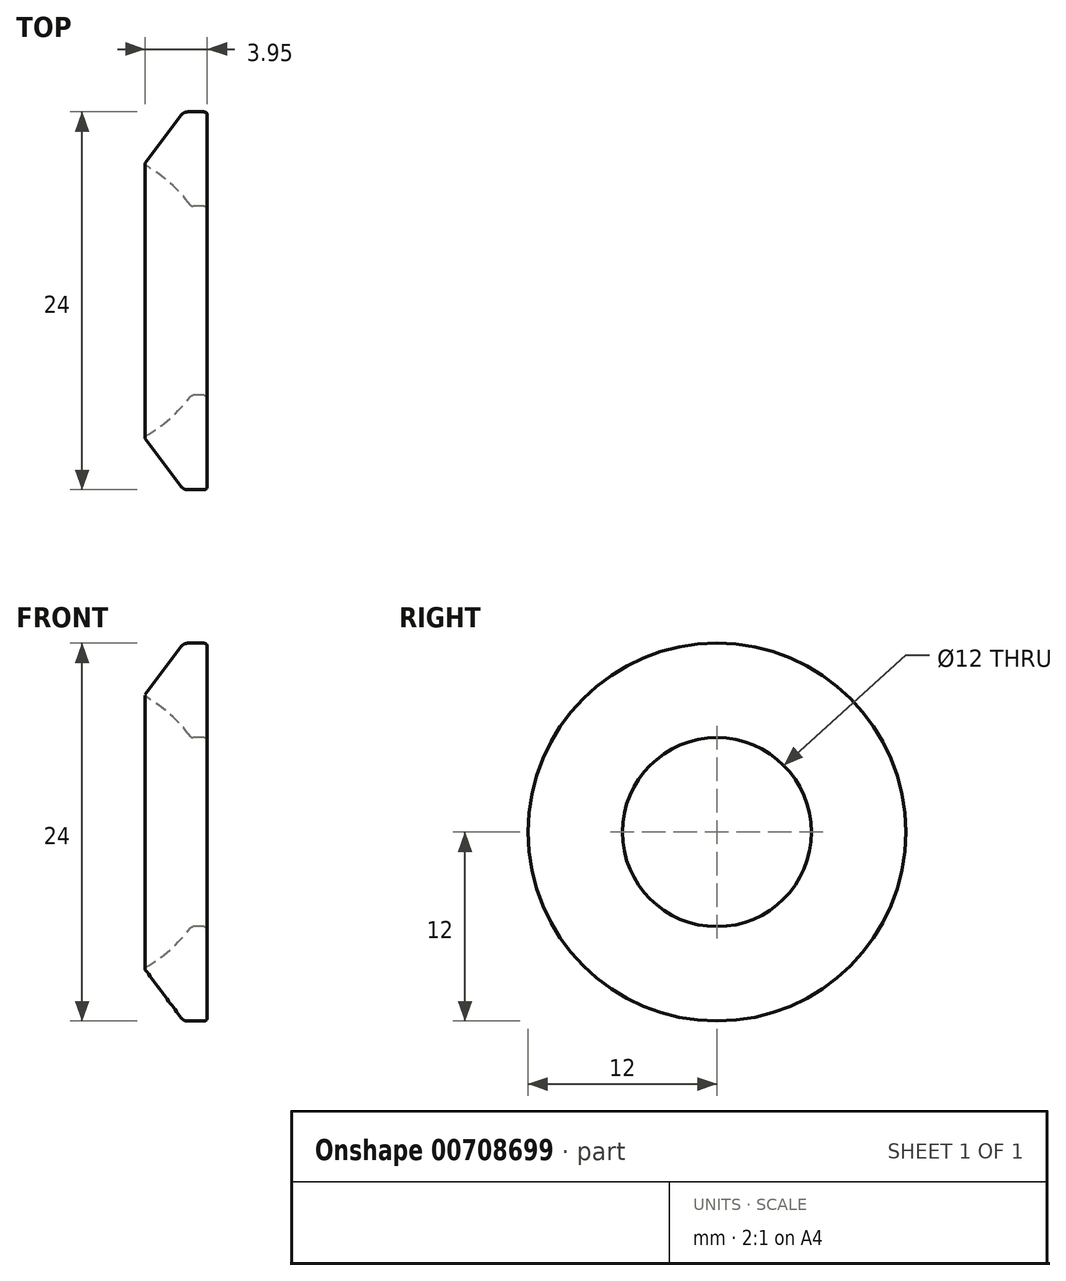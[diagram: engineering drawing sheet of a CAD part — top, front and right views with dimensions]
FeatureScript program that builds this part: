
annotation { "Feature Type Name" : "Feature", "Feature Type Description" : "" }
export const myFeature = defineFeature(function(context is Context, id is Id, definition is map)
    precondition{}
    {
        {
            var Q0;
            Q0=qCreatedBy(makeId("Front.planeOp"),FACE);
            var sketch = newSketch(context, id + "F0", { "sketchPlane" : qUnion([Q0])});
            skLineSegment(sketch, "E0", {"start": v(-1, 6) * mm, "end": v(0, 6) * mm});
            skLineSegment(sketch, "E1", {"start": v(0, 6) * mm, "end": v(0, 12) * mm});
            skLineSegment(sketch, "E2", {"start": v(0, 12) * mm, "end": v(-1.5, 12) * mm});
            skLineSegment(sketch, "E3", {"start": v(-1.5, 12) * mm, "end": v(-4, 8.66) * mm});
            skArc(sketch, "E4", {"start": v(-4, 8.66) * mm, "mid": v(-2.37, 7.48) * mm, "end": v(-1, 6) * mm});
            skLineSegment(sketch, "E5", {"start": v(-16.9, 0) * mm, "end": v(12.5, 0) * mm, "construction": true});
            skSolve(sketch);
        }
        {
            var Q0;
            Q0=makeQuery(id+"F0.imprint","IMPRINT",FACE,{"disambiguationData":[TD([[makeQuery(id+"F0.imprint","IMPRINT",EDGE,{"derivedFrom":sQuery(id+"F0.wireOp",EDGE,"E0")}),1.0]])]});
            var Q1;
            Q1=sQuery(id+"F0.wireOp",EDGE,"E5");
            revolve(context, id + "F1", {"surfaceOperationType" : NewSurfaceOperationType.NEW, "entities" : qUnion([Q0]), "axis" : qUnion([Q1]), "revolveType" : RevolveType.FULL});
        }
        {
            var Q0;
            Q0=makeQuery(id+"F1.opRevolve","SWEPT_EDGE",EDGE,{"disambiguationData":[OSD([sQuery(id+"F0.wireOp",EDGE,"E0"),sQuery(id+"F0.wireOp",EDGE,"E4")])]});
            fillet(context, id + "F2", {"entities" : qUnion([Q0]), "radius" : 0.2 * mm, "tangentPropagation" : true, "allowEdgeOverflow" : false});
        }
        {
            var Q0;
            Q0=makeQuery(id+"F1.opRevolve","SWEPT_EDGE",EDGE,{"disambiguationData":[OSD([sQuery(id+"F0.wireOp",EDGE,"E2"),sQuery(id+"F0.wireOp",EDGE,"E3")])]});
            fillet(context, id + "F3", {"entities" : qUnion([Q0]), "radius" : 0.5 * mm, "tangentPropagation" : true, "allowEdgeOverflow" : false});
        }
        {
            var Q0;
            Q0=makeQuery(id+"F1.opRevolve","SWEPT_EDGE",EDGE,{"disambiguationData":[OSD([sQuery(id+"F0.wireOp",EDGE,"E1"),sQuery(id+"F0.wireOp",EDGE,"E2")])]});
            fillet(context, id + "F4", {"entities" : qUnion([Q0]), "radius" : 0.2 * mm, "tangentPropagation" : true, "allowEdgeOverflow" : false});
        }
        {
            var Q0;
            Q0=makeQuery(id+"F1.opRevolve","SWEPT_EDGE",EDGE,{"disambiguationData":[OSD([sQuery(id+"F0.wireOp",EDGE,"E3"),sQuery(id+"F0.wireOp",EDGE,"E4")])]});
            fillet(context, id + "F5", {"entities" : qUnion([Q0]), "radius" : 0.1 * mm, "tangentPropagation" : true, "allowEdgeOverflow" : false});
        }
        {
            var Q0;
            Q0=makeQuery(id+"F1.opRevolve","SWEPT_EDGE",EDGE,{"disambiguationData":[OSD([sQuery(id+"F0.wireOp",EDGE,"E0"),sQuery(id+"F0.wireOp",EDGE,"E1")])]});
            fillet(context, id + "F6", {"entities" : qUnion([Q0]), "radius" : 0.2 * mm, "tangentPropagation" : true, "allowEdgeOverflow" : false});
        }
    });
